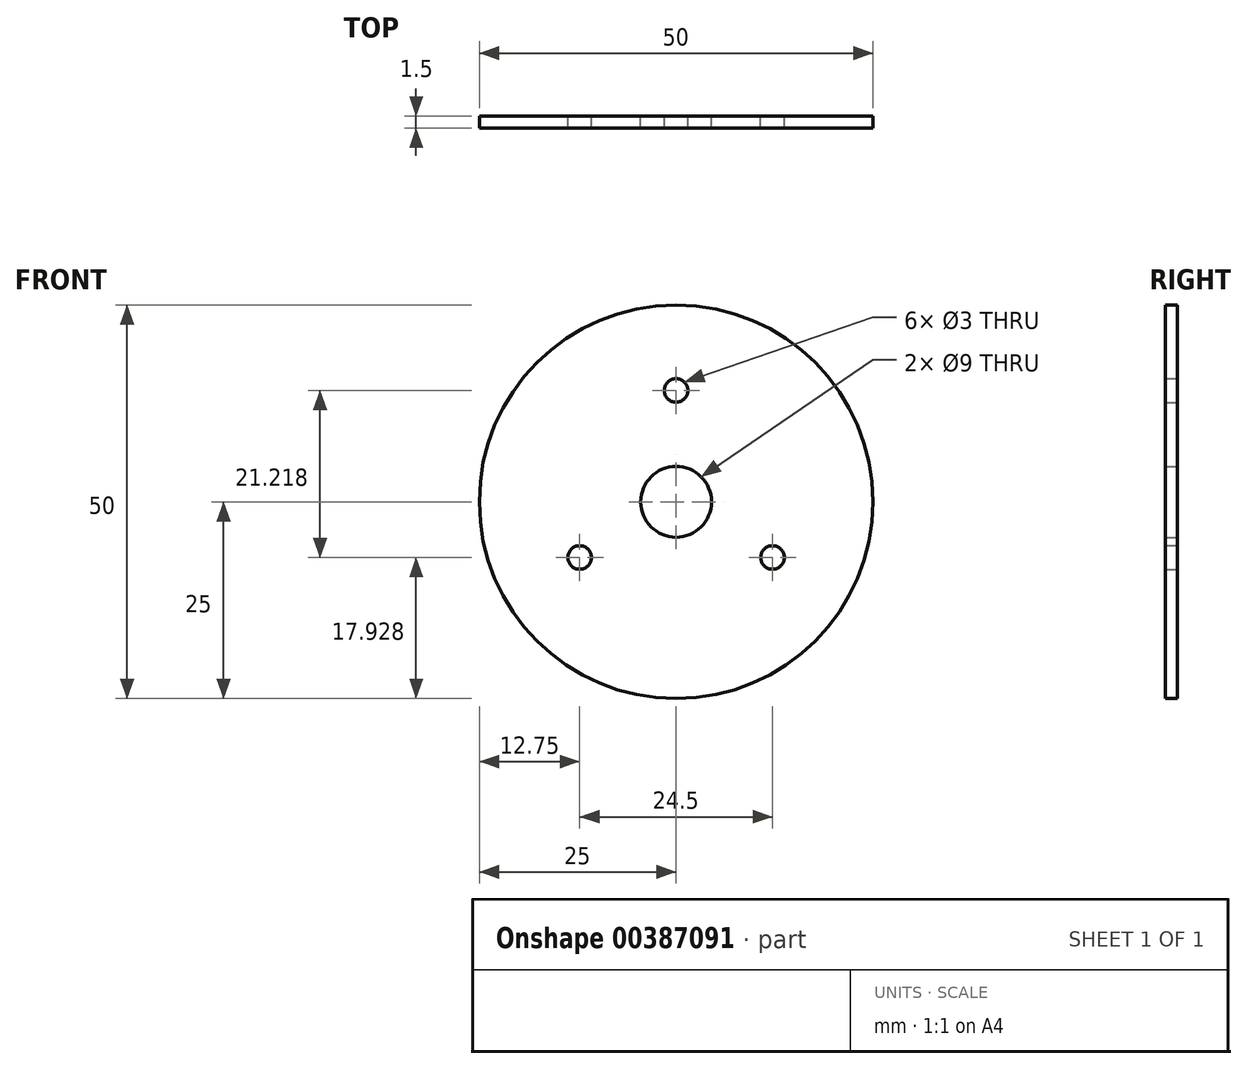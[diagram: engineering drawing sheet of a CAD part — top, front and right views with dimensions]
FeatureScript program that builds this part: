
annotation { "Feature Type Name" : "Feature", "Feature Type Description" : "" }
export const myFeature = defineFeature(function(context is Context, id is Id, definition is map)
    precondition{}
    {
        {
            var Q0;
            Q0=qCreatedBy(makeId("Front.planeOp"),FACE);
            var sketch = newSketch(context, id + "F0", { "sketchPlane" : qUnion([Q0])});
            skCircle(sketch, "E0", {"center": v(0, 0) * mm, "radius": 4.5 * mm});
            skCircle(sketch, "E1", {"center": v(0, 14.15) * mm, "radius": 1.5 * mm});
            skCircle(sketch, "E2", {"center": v(-12.25, -7.07) * mm, "radius": 1.5 * mm});
            skCircle(sketch, "E3", {"center": v(12.25, -7.07) * mm, "radius": 1.5 * mm});
            skCircle(sketch, "E4", {"center": v(0, 0) * mm, "radius": 25 * mm});
            skSolve(sketch);
        }
        {
            var Q0;
            Q0 = qSketchRegion(id + "F0", true);
            extrude(context, id + "F1", {"entities" : qUnion([Q0]), "depth" : 1.5 * mm});
        }
    });
